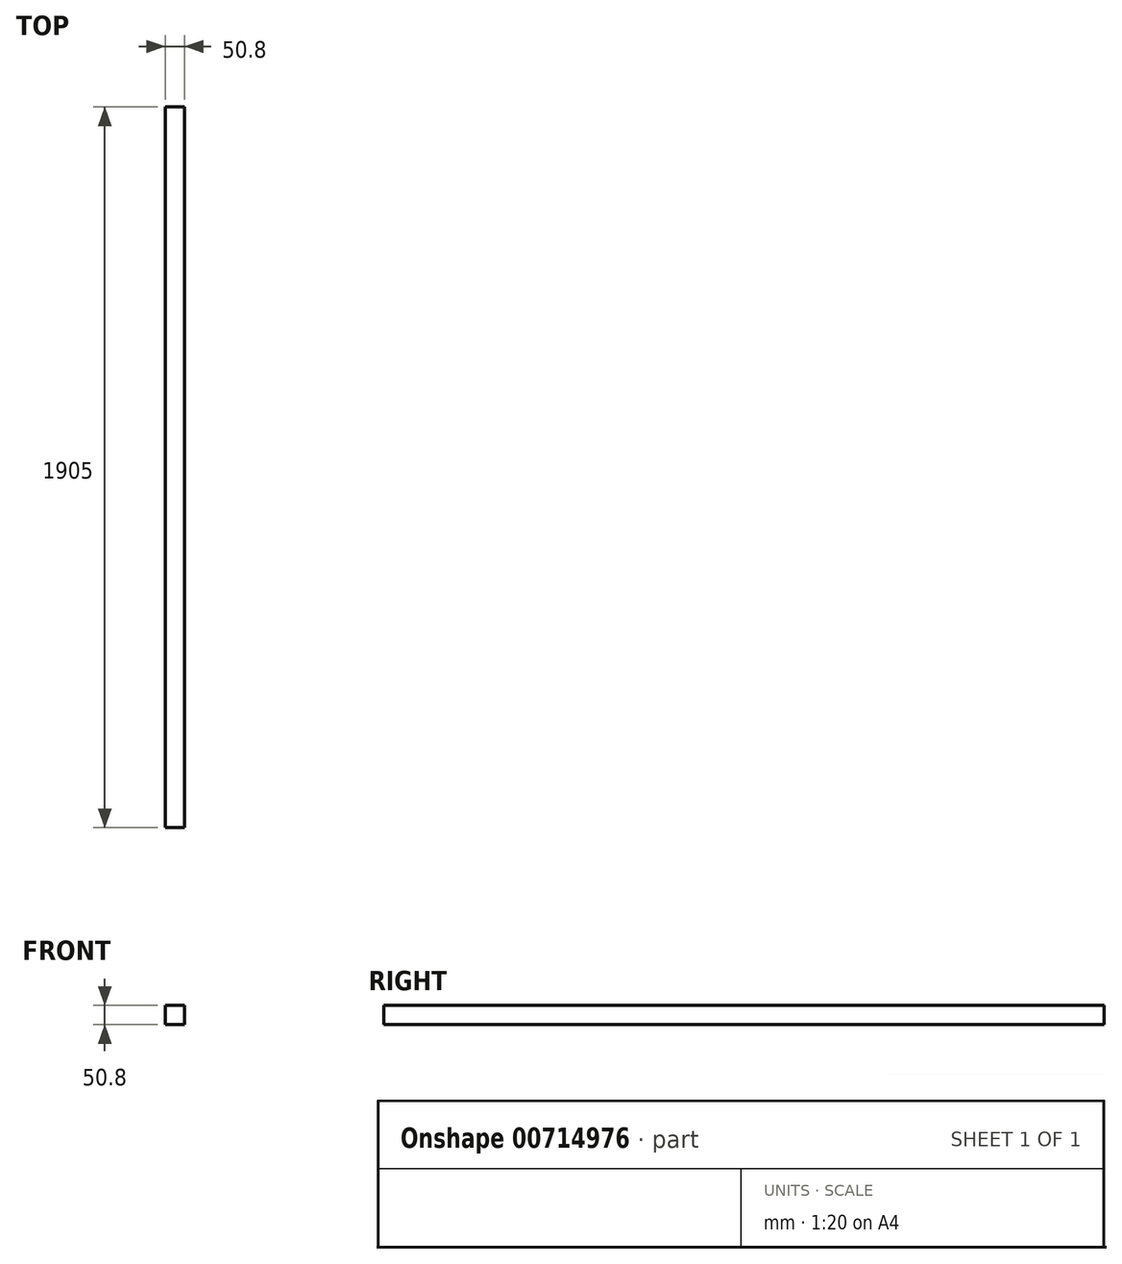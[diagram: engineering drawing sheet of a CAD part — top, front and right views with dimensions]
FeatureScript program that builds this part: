
annotation { "Feature Type Name" : "Feature", "Feature Type Description" : "" }
export const myFeature = defineFeature(function(context is Context, id is Id, definition is map)
    precondition{}
    {
        {
            var Q0;
            Q0=qCreatedBy(makeId("Right.planeOp"),FACE);
            var sketch = newSketch(context, id + "F0", { "sketchPlane" : qUnion([Q0])});
            skLineSegment(sketch, "E0.bottom", {"start": v(1905, 50.8) * mm, "end": v(0, 50.8) * mm});
            skLineSegment(sketch, "E0.top", {"start": v(1905, 0) * mm, "end": v(0, 0) * mm});
            skLineSegment(sketch, "E0.left", {"start": v(1905, 50.8) * mm, "end": v(1905, 0) * mm});
            skLineSegment(sketch, "E0.right", {"start": v(0, 50.8) * mm, "end": v(0, 0) * mm});
            skSolve(sketch);
        }
        {
            var Q0;
            Q0=makeQuery(id+"F0.imprint","IMPRINT",FACE,{"disambiguationData":[TD([[makeQuery(id+"F0.imprint","IMPRINT",EDGE,{"derivedFrom":sQuery(id+"F0.wireOp",EDGE,"E0.bottom")}),1.0]])]});
            extrude(context, id + "F1", {"entities" : qUnion([Q0]), "depth" : 50.8 * mm, "offsetDistance" : 25.4 * mm});
        }
    });
